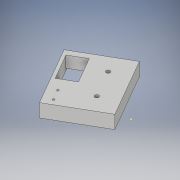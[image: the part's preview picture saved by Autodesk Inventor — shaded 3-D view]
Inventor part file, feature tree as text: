
AUTODESK INVENTOR PART (.ipt)
format: ipt  version: 2017 (Build 210142000, 142)  size: 223,232 bytes
history: native  units: in
note: dims shown in document units (in); Inventor stores cm internally (conversion verified against a paired STEP export)
features: sketch x7, extrude x6, projected_geometry x5, imported_body x1
ambient origin geometry x8: Origin, YZ Plane, XZ Plane, XY Plane, X Axis, Y Axis, Z Axis, Center Point
bodies: Solid1 (feature_tree)
feature tree (19):
  extrude  "Extrusion1"  Depth=0.3937in TaperAngle=0.0deg
  extrude  "Extrusion2"  Depth=0.3937in TaperAngle=0.0deg
  extrude  "Extrusion4"  Depth=0.3937in TaperAngle=0.0deg
  extrude  "Extrusion5"  Depth=0.3937in TaperAngle=0.0deg
  extrude  "Extrusion6"  Depth=0.188in
  extrude  "limit switch"  Depth=0.125in
  sketch  "Sketch9"  dims[d19=0.3937in d20=0.0in d21=0.276in d22=0.2in d23=0.575in d24=0.063in d25=0.3937in d26=0.0in]
  sketch  "Sketch1"  dims[d0=1.25in d1=0.3937in d2=0.0in]
  projected_geometry  "Projected Loop1"
  sketch  "Sketch2"  dims[d3=0.125in d4=0.3937in d5=0.0in]
  sketch  "Sketch4"  dims[d9=0.4331in d10=0.3937in d11=0.0in]
  projected_geometry  "Projected Loop3"
  sketch  "Sketch5"  dims[d12=0.3937in d13=0.3937in d14=0.0in]
  projected_geometry  "Projected Loop4"
  sketch  "Sketch6"  dims[d15=0.765in d16=0.188in]
  projected_geometry  "Projected Loop5"
  sketch  "Sketch7"  dims[d17=0.5in d18=0.125in]
  projected_geometry  "Projected Loop6"
  imported_body  "Base1"
